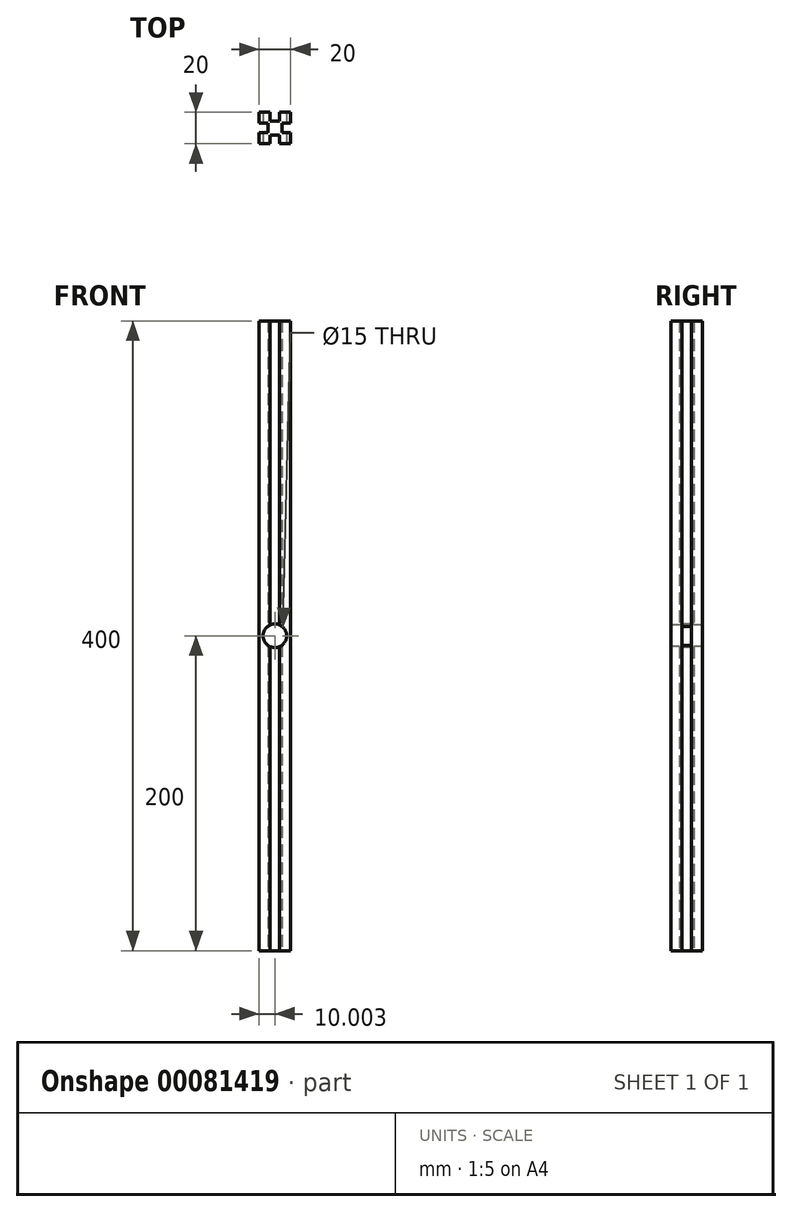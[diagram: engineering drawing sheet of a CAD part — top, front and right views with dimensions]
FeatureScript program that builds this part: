
annotation { "Feature Type Name" : "Feature", "Feature Type Description" : "" }
export const myFeature = defineFeature(function(context is Context, id is Id, definition is map)
    precondition{}
    {
        {
            var Q0;
            Q0=qCreatedBy(makeId("Top.planeOp"),FACE);
            var sketch = newSketch(context, id + "F0", { "sketchPlane" : qUnion([Q0])});
            skLineSegment(sketch, "E0.bottom", {"start": v(-87.17, -55.96) * mm, "end": v(-67.17, -55.96) * mm});
            skLineSegment(sketch, "E0.top", {"start": v(-87.17, -35.96) * mm, "end": v(-67.17, -35.96) * mm});
            skLineSegment(sketch, "E0.left", {"start": v(-87.17, -55.96) * mm, "end": v(-87.17, -35.96) * mm});
            skLineSegment(sketch, "E0.right", {"start": v(-67.17, -55.96) * mm, "end": v(-67.17, -35.96) * mm});
            skLineSegment(sketch, "E1.bottom", {"start": v(-80.17, -35.96) * mm, "end": v(-74.17, -35.96) * mm});
            skLineSegment(sketch, "E1.top", {"start": v(-80.17, -41.46) * mm, "end": v(-74.17, -41.46) * mm});
            skLineSegment(sketch, "E1.left", {"start": v(-80.17, -35.96) * mm, "end": v(-80.17, -41.46) * mm});
            skLineSegment(sketch, "E1.right", {"start": v(-74.17, -35.96) * mm, "end": v(-74.17, -41.46) * mm});
            skLineSegment(sketch, "E2.bottom", {"start": v(-67.17, -42.96) * mm, "end": v(-72.67, -42.96) * mm});
            skLineSegment(sketch, "E2.top", {"start": v(-67.17, -48.96) * mm, "end": v(-72.67, -48.96) * mm});
            skLineSegment(sketch, "E2.left", {"start": v(-67.17, -42.96) * mm, "end": v(-67.17, -48.96) * mm});
            skLineSegment(sketch, "E2.right", {"start": v(-72.67, -42.96) * mm, "end": v(-72.67, -48.96) * mm});
            skLineSegment(sketch, "E3.bottom", {"start": v(-74.17, -55.96) * mm, "end": v(-80.17, -55.96) * mm});
            skLineSegment(sketch, "E3.top", {"start": v(-74.17, -50.46) * mm, "end": v(-80.17, -50.46) * mm});
            skLineSegment(sketch, "E3.left", {"start": v(-74.17, -55.96) * mm, "end": v(-74.17, -50.46) * mm});
            skLineSegment(sketch, "E3.right", {"start": v(-80.17, -55.96) * mm, "end": v(-80.17, -50.46) * mm});
            skLineSegment(sketch, "E4.bottom", {"start": v(-87.17, -48.96) * mm, "end": v(-81.67, -48.96) * mm});
            skLineSegment(sketch, "E4.top", {"start": v(-87.17, -42.96) * mm, "end": v(-81.67, -42.96) * mm});
            skLineSegment(sketch, "E4.left", {"start": v(-87.17, -48.96) * mm, "end": v(-87.17, -42.96) * mm});
            skLineSegment(sketch, "E4.right", {"start": v(-81.67, -48.96) * mm, "end": v(-81.67, -42.96) * mm});
            skSolve(sketch);
        }
        {
            var Q0;
            Q0=makeQuery(id+"F0.imprint","IMPRINT",FACE,{"disambiguationData":[TD([[makeQuery(id+"F0.imprint","IMPRINT",EDGE,{"derivedFrom":sQuery(id+"F0.wireOp",EDGE,"E1.top")}),-1.0]])]});
            extrude(context, id + "F1", {"entities" : qUnion([Q0]), "depth" : 400 * mm});
        }
        {
            var Q0;
            Q0=makeQuery(id+"F1.opExtrude","SWEPT_FACE",FACE,{"disambiguationData":[OSD([sQuery(id+"F0.wireOp",EDGE,"E3.top")])]});
            var sketch = newSketch(context, id + "F2", { "sketchPlane" : qUnion([Q0])});
            skCircle(sketch, "E5", {"center": v(-77.17, 200) * mm, "radius": 7.5 * mm});
            skPoint(sketch, "E6", {"position": v(-80.17, 200) * mm});
            skPoint(sketch, "E7", {"position": v(-77.17, 400) * mm});
            skSolve(sketch);
        }
        {
            var Q0;
            Q0 = qSketchRegion(id + "F2", true);
            extrude(context, id + "F3", {"entities" : qUnion([Q0]), "operationType" : NewBodyOperationType.REMOVE, "endBound" : BoundingType.SYMMETRIC, "oppositeDirection" : true, "depth" : 50 * mm});
        }
    });
